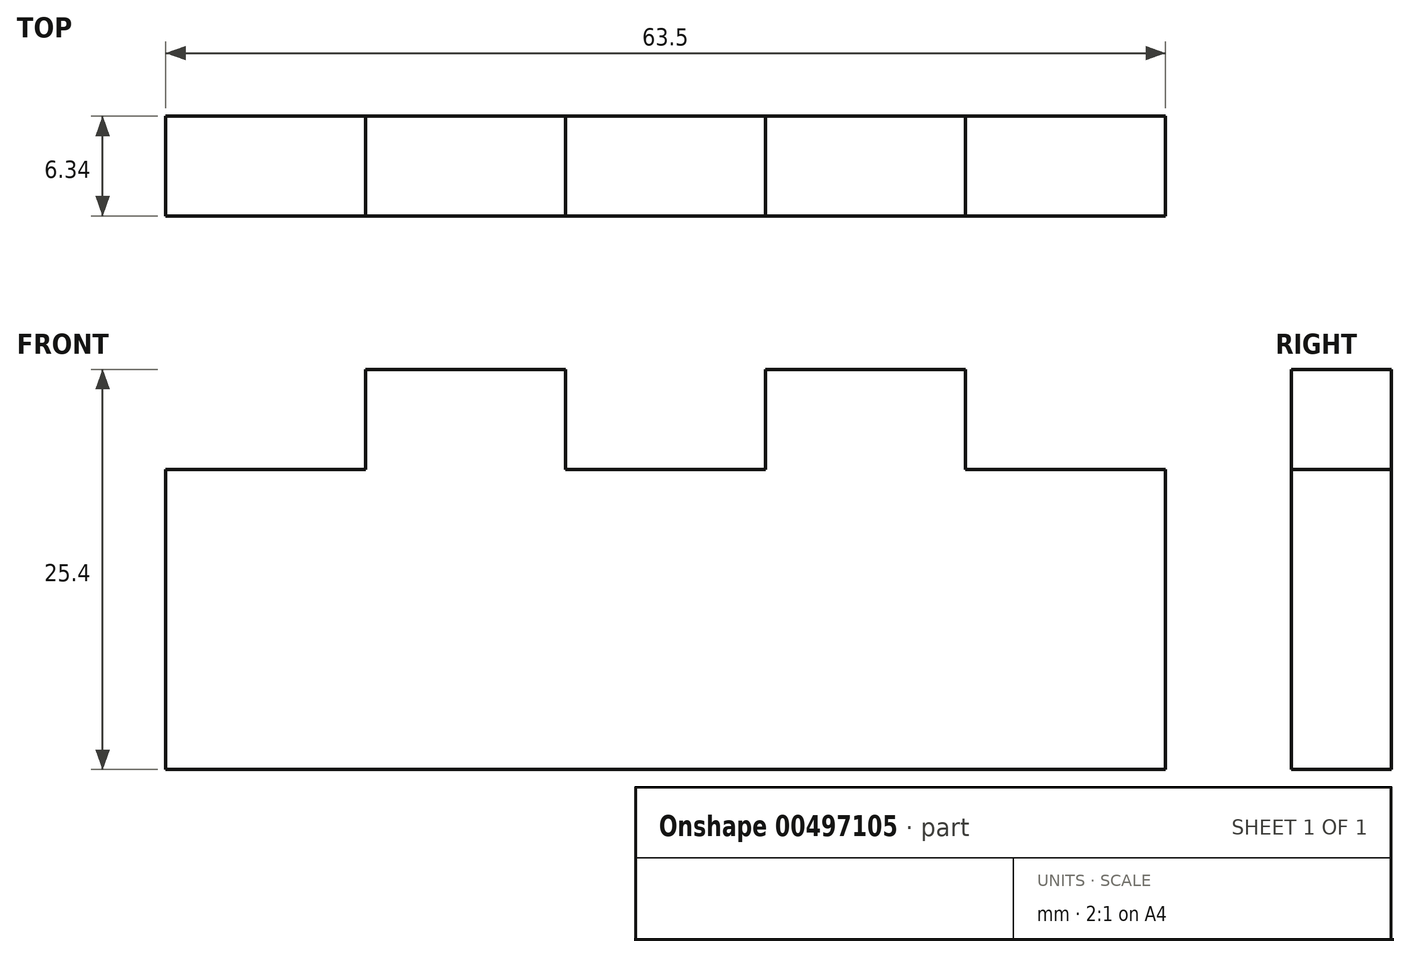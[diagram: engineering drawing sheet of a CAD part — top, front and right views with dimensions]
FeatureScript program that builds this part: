
annotation { "Feature Type Name" : "Feature", "Feature Type Description" : "" }
export const myFeature = defineFeature(function(context is Context, id is Id, definition is map)
    precondition{}
    {
        {
            var Q0;
            Q0=qCreatedBy(makeId("Top.planeOp"),FACE);
            var sketch = newSketch(context, id + "F0", { "sketchPlane" : qUnion([Q0])});
            skLineSegment(sketch, "E0.bottom", {"start": v(31.75, -3.17) * mm, "end": v(-31.75, -3.18) * mm});
            skLineSegment(sketch, "E0.top", {"start": v(31.75, 3.18) * mm, "end": v(-31.75, 3.17) * mm});
            skLineSegment(sketch, "E0.left", {"start": v(31.75, -3.17) * mm, "end": v(31.75, 3.18) * mm});
            skLineSegment(sketch, "E0.right", {"start": v(-31.75, -3.18) * mm, "end": v(-31.75, 3.17) * mm});
            skPoint(sketch, "E0.middle", {"position": v(0, 0) * mm});
            skSolve(sketch);
        }
        {
            var Q0;
            Q0=makeQuery(id+"F0.imprint","IMPRINT",FACE,{"disambiguationData":[TD([[makeQuery(id+"F0.imprint","IMPRINT",EDGE,{"derivedFrom":sQuery(id+"F0.wireOp",EDGE,"E0.bottom")}),-1.0]])]});
            extrude(context, id + "F1", {"entities" : qUnion([Q0]), "depth" : 19.05 * mm});
        }
        {
            var Q0;
            Q0=makeQuery(id+"F1.opExtrude","CAP_FACE",FACE,{"disambiguationData":[OSD([sQuery(id+"F0.wireOp",EDGE,"E0.bottom"),sQuery(id+"F0.wireOp",EDGE,"E0.top"),sQuery(id+"F0.wireOp",EDGE,"E0.left"),sQuery(id+"F0.wireOp",EDGE,"E0.right")])],"isStart":false});
            var sketch = newSketch(context, id + "F2", { "sketchPlane" : qUnion([Q0])});
            skLineSegment(sketch, "E1.bottom", {"start": v(-19.05, -3.18) * mm, "end": v(-6.35, -3.18) * mm});
            skLineSegment(sketch, "E1.top", {"start": v(-19.05, 3.18) * mm, "end": v(-6.35, 3.18) * mm});
            skLineSegment(sketch, "E1.left", {"start": v(-19.05, -3.18) * mm, "end": v(-19.05, 3.18) * mm});
            skLineSegment(sketch, "E1.right", {"start": v(-6.35, -3.18) * mm, "end": v(-6.35, 3.18) * mm});
            skLineSegment(sketch, "E2.bottom", {"start": v(19.05, -3.17) * mm, "end": v(6.35, -3.17) * mm});
            skLineSegment(sketch, "E2.top", {"start": v(19.05, 3.18) * mm, "end": v(6.35, 3.18) * mm});
            skLineSegment(sketch, "E2.left", {"start": v(19.05, -3.17) * mm, "end": v(19.05, 3.18) * mm});
            skLineSegment(sketch, "E2.right", {"start": v(6.35, -3.18) * mm, "end": v(6.35, 3.18) * mm});
            skSolve(sketch);
        }
        {
            var Q0;
            Q0=makeQuery(id+"F2.imprint","IMPRINT",FACE,{"disambiguationData":[TD([[makeQuery(id+"F2.imprint","IMPRINT",EDGE,{"derivedFrom":sQuery(id+"F2.wireOp",EDGE,"E1.bottom")}),-1.0]])]});
            var Q1;
            Q1=makeQuery(id+"F2.imprint","IMPRINT",FACE,{"disambiguationData":[TD([[makeQuery(id+"F2.imprint","IMPRINT",EDGE,{"derivedFrom":sQuery(id+"F2.wireOp",EDGE,"E2.bottom")}),-1.0]])]});
            extrude(context, id + "F3", {"entities" : qUnion([Q0, Q1]), "operationType" : NewBodyOperationType.ADD, "depth" : 6.35 * mm});
        }
    });
